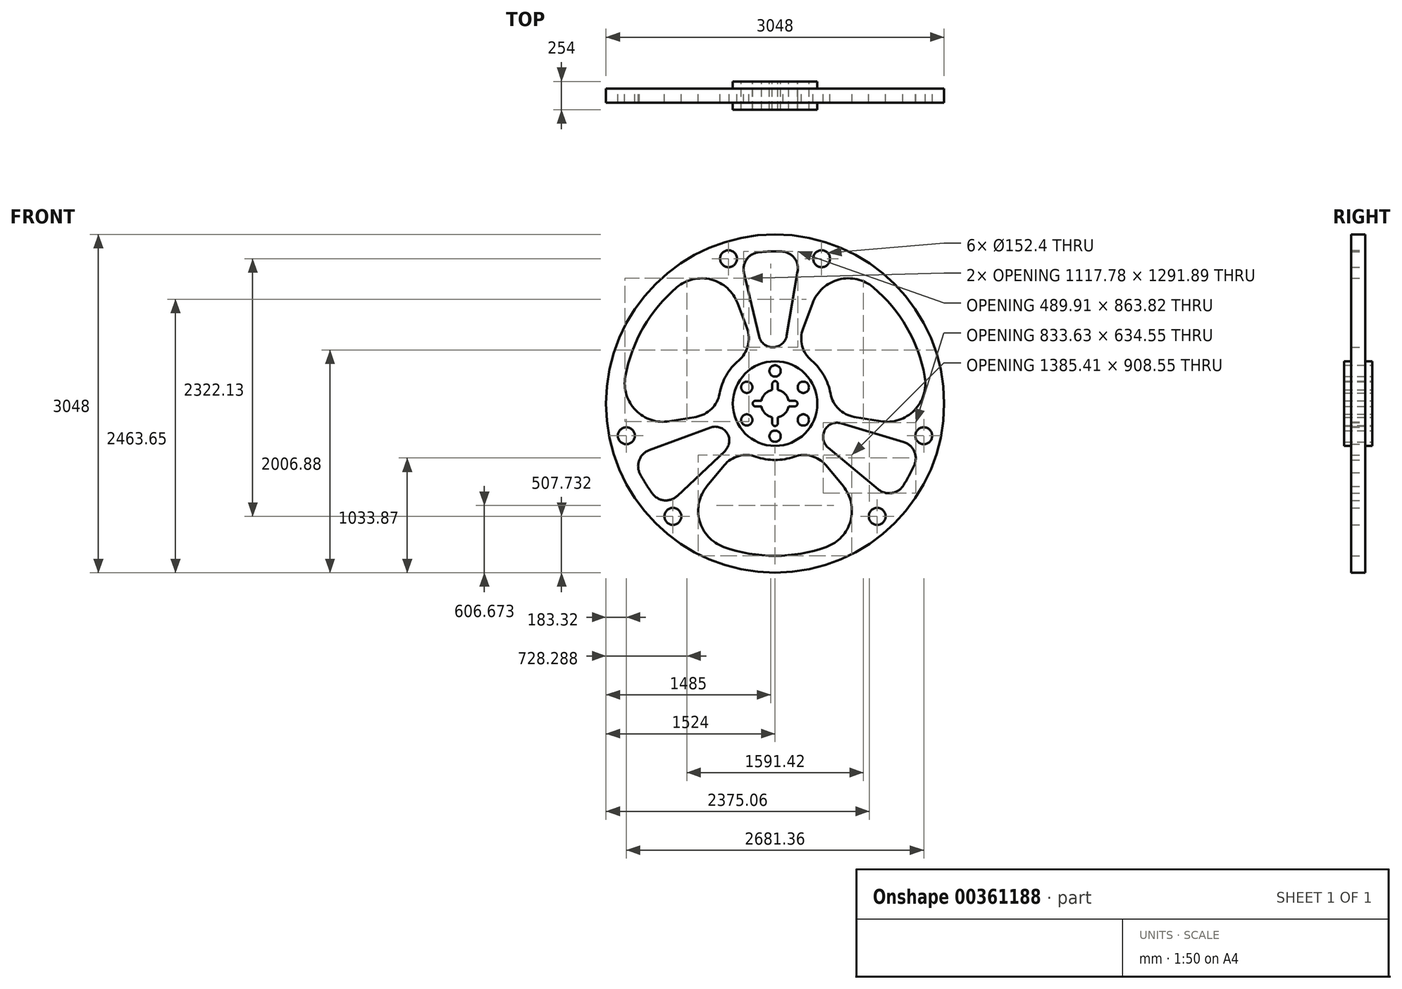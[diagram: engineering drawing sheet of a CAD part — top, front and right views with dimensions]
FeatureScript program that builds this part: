
annotation { "Feature Type Name" : "Feature", "Feature Type Description" : "" }
export const myFeature = defineFeature(function(context is Context, id is Id, definition is map)
    precondition{}
    {
        {
            var Q0;
            Q0=qCreatedBy(makeId("Front.planeOp"),FACE);
            var sketch = newSketch(context, id + "F0", { "sketchPlane" : qUnion([Q0])});
            skCircle(sketch, "E0", {"center": v(0, 0) * mm, "radius": 1524 * mm});
            skLineSegment(sketch, "E1", {"start": v(-143.94, 605.3) * mm, "end": v(-279.86, 1176.82) * mm});
            skLineSegment(sketch, "E2", {"start": v(104.8, 613.28) * mm, "end": v(203.6, 1191.45) * mm});
            skArc(sketch, "E3", {"start": v(-148.04, 1363.59) * mm, "mid": v(-256.1, 1299.96) * mm, "end": v(-279.86, 1176.82) * mm});
            skArc(sketch, "E4.trimOffspring", {"start": v(203.6, 1191.45) * mm, "mid": v(176.34, 1308.8) * mm, "end": v(72.38, 1369.69) * mm});
            skArc(sketch, "E5.trimOffspring", {"start": v(72.38, 1369.69) * mm, "mid": v(-37.95, 1371.07) * mm, "end": v(-148.04, 1363.59) * mm});
            skArc(sketch, "E6", {"start": v(-143.94, 605.3) * mm, "mid": v(-16.31, 507.74) * mm, "end": v(104.8, 613.28) * mm});
            skArc(sketch, "E7", {"start": v(-328.23, 387.72) * mm, "mid": v(-439.94, 254) * mm, "end": v(-499.9, 90.4) * mm});
            skArc(sketch, "E8", {"start": v(-25.4, 123.15) * mm, "mid": v(-88.91, 88.91) * mm, "end": v(-123.15, 25.4) * mm});
            skCircle(sketch, "E9", {"center": v(-419.55, 1305.86) * mm, "radius": 76.2 * mm});
            skCircle(sketch, "E10", {"center": v(419.55, 1305.86) * mm, "radius": 76.2 * mm});
            skCircle(sketch, "E11.1.0", {"center": v(-1340.68, -289.6) * mm, "radius": 76.2 * mm});
            skCircle(sketch, "E11.1.1", {"center": v(-921.13, -1016.27) * mm, "radius": 76.2 * mm});
            skLineSegment(sketch, "E11.1.2", {"start": v(-452.23, -427.3) * mm, "end": v(-879.23, -830.77) * mm});
            skLineSegment(sketch, "E11.1.3", {"start": v(-583.52, -215.88) * mm, "end": v(-1133.62, -419.4) * mm});
            skArc(sketch, "E11.1.4", {"start": v(-1133.62, -419.4) * mm, "mid": v(-1221.62, -501.69) * mm, "end": v(-1222.38, -622.16) * mm});
            skArc(sketch, "E11.1.5", {"start": v(-1222.38, -622.16) * mm, "mid": v(-1168.4, -718.4) * mm, "end": v(-1106.88, -810) * mm});
            skArc(sketch, "E11.1.6", {"start": v(-1106.88, -810) * mm, "mid": v(-997.74, -871.77) * mm, "end": v(-879.23, -830.77) * mm});
            skArc(sketch, "E11.1.7", {"start": v(-452.23, -427.3) * mm, "mid": v(-431.56, -268) * mm, "end": v(-583.52, -215.88) * mm});
            skCircle(sketch, "E11.2.0", {"center": v(921.13, -1016.27) * mm, "radius": 76.2 * mm});
            skCircle(sketch, "E11.2.1", {"center": v(1340.68, -289.6) * mm, "radius": 76.2 * mm});
            skLineSegment(sketch, "E11.2.2", {"start": v(596.17, -177.99) * mm, "end": v(1159.08, -346.05) * mm});
            skLineSegment(sketch, "E11.2.3", {"start": v(478.72, -397.4) * mm, "end": v(930.03, -772.04) * mm});
            skArc(sketch, "E11.2.4", {"start": v(930.03, -772.04) * mm, "mid": v(1045.29, -807.11) * mm, "end": v(1150, -747.53) * mm});
            skArc(sketch, "E11.2.5", {"start": v(1150, -747.53) * mm, "mid": v(1206.36, -652.67) * mm, "end": v(1254.92, -553.59) * mm});
            skArc(sketch, "E11.2.6", {"start": v(1254.92, -553.59) * mm, "mid": v(1253.85, -428.19) * mm, "end": v(1159.08, -346.05) * mm});
            skArc(sketch, "E11.2.7", {"start": v(596.17, -177.99) * mm, "mid": v(447.87, -239.74) * mm, "end": v(478.72, -397.4) * mm});
            skArc(sketch, "E12", {"start": v(459.34, -557.22) * mm, "mid": v(328.02, -472.14) * mm, "end": v(171.66, -478.12) * mm});
            skPoint(sketch, "E13.centerSnap0", {"position": v(0, -964.87) * mm});
            skArc(sketch, "E14", {"start": v(-613.73, -744.52) * mm, "mid": v(-680.45, -1056.72) * mm, "end": v(-463.49, -1290.92) * mm});
            skArc(sketch, "E15.trimOffspring", {"start": v(463.49, -1290.92) * mm, "mid": v(680.45, -1056.72) * mm, "end": v(613.73, -744.52) * mm});
            skArc(sketch, "E16.trimOffspring", {"start": v(-171.66, -478.12) * mm, "mid": v(-328.02, -472.14) * mm, "end": v(-459.34, -557.22) * mm});
            skArc(sketch, "E17.trimOffspring", {"start": v(-463.49, -1290.92) * mm, "mid": v(0, -1371.6) * mm, "end": v(463.49, -1290.92) * mm});
            skLineSegment(sketch, "E18.trimOffspring", {"start": v(-459.34, -557.22) * mm, "end": v(-613.73, -744.52) * mm});
            skLineSegment(sketch, "E19.trimOffspring", {"start": v(459.34, -557.22) * mm, "end": v(613.73, -744.52) * mm});
            skArc(sketch, "E20.1.0", {"start": v(951.64, -159.25) * mm, "mid": v(1255.37, -60.93) * mm, "end": v(1349.71, 244.07) * mm});
            skLineSegment(sketch, "E20.1.1", {"start": v(712.24, -119.19) * mm, "end": v(951.64, -159.25) * mm});
            skArc(sketch, "E20.1.2", {"start": v(499.9, 90.4) * mm, "mid": v(572.9, -48) * mm, "end": v(712.24, -119.19) * mm});
            skArc(sketch, "E20.1.3", {"start": v(252.9, 676.4) * mm, "mid": v(244.88, 520.14) * mm, "end": v(328.23, 387.72) * mm});
            skLineSegment(sketch, "E20.1.4", {"start": v(252.9, 676.4) * mm, "end": v(337.9, 903.77) * mm});
            skArc(sketch, "E20.1.5", {"start": v(1349.71, 244.07) * mm, "mid": v(1187.84, 685.8) * mm, "end": v(886.22, 1046.85) * mm});
            skArc(sketch, "E20.1.6", {"start": v(886.22, 1046.85) * mm, "mid": v(574.92, 1117.65) * mm, "end": v(337.9, 903.77) * mm});
            skArc(sketch, "E20.2.0", {"start": v(-337.9, 903.77) * mm, "mid": v(-574.92, 1117.65) * mm, "end": v(-886.22, 1046.85) * mm});
            skLineSegment(sketch, "E20.2.1", {"start": v(-252.9, 676.4) * mm, "end": v(-337.9, 903.77) * mm});
            skArc(sketch, "E20.2.2", {"start": v(-328.23, 387.72) * mm, "mid": v(-244.88, 520.14) * mm, "end": v(-252.9, 676.4) * mm});
            skArc(sketch, "E20.2.3", {"start": v(-712.24, -119.19) * mm, "mid": v(-572.9, -48) * mm, "end": v(-499.9, 90.4) * mm});
            skLineSegment(sketch, "E20.2.4", {"start": v(-712.24, -119.19) * mm, "end": v(-951.64, -159.25) * mm});
            skArc(sketch, "E20.2.5", {"start": v(-886.22, 1046.85) * mm, "mid": v(-1187.84, 685.8) * mm, "end": v(-1349.71, 244.07) * mm});
            skArc(sketch, "E20.2.6", {"start": v(-1349.71, 244.07) * mm, "mid": v(-1255.37, -60.93) * mm, "end": v(-951.64, -159.25) * mm});
            skArc(sketch, "E21.trimOffspring", {"start": v(499.9, 90.4) * mm, "mid": v(439.94, 254) * mm, "end": v(328.23, 387.72) * mm});
            skArc(sketch, "E22.trimOffspring", {"start": v(-171.66, -478.12) * mm, "mid": v(0, -508) * mm, "end": v(171.66, -478.12) * mm});
            skCircle(sketch, "E23", {"center": v(0, 0) * mm, "radius": 381 * mm});
            skCircle(sketch, "E24", {"center": v(0, 294.12) * mm, "radius": 50.8 * mm});
            skCircle(sketch, "E25.1.0", {"center": v(-254.72, 147.06) * mm, "radius": 50.8 * mm});
            skCircle(sketch, "E25.2.0", {"center": v(-254.72, -147.06) * mm, "radius": 50.8 * mm});
            skCircle(sketch, "E25.3.0", {"center": v(0, -294.12) * mm, "radius": 50.8 * mm});
            skCircle(sketch, "E25.4.0", {"center": v(254.72, -147.06) * mm, "radius": 50.8 * mm});
            skCircle(sketch, "E25.5.0", {"center": v(254.72, 147.06) * mm, "radius": 50.8 * mm});
            skArc(sketch, "E26", {"start": v(25.4, 176.54) * mm, "mid": v(0, 201.94) * mm, "end": v(-25.4, 176.54) * mm});
            skLineSegment(sketch, "E27", {"start": v(-25.4, 176.54) * mm, "end": v(-25.4, 123.15) * mm});
            skLineSegment(sketch, "E28", {"start": v(25.4, 176.54) * mm, "end": v(25.4, 123.15) * mm});
            skArc(sketch, "E29.1.0", {"start": v(-176.54, 25.4) * mm, "mid": v(-201.94, 0) * mm, "end": v(-176.54, -25.4) * mm});
            skLineSegment(sketch, "E29.1.1", {"start": v(-176.54, -25.4) * mm, "end": v(-123.15, -25.4) * mm});
            skLineSegment(sketch, "E29.1.2", {"start": v(-176.54, 25.4) * mm, "end": v(-123.15, 25.4) * mm});
            skArc(sketch, "E29.2.0", {"start": v(-25.4, -176.54) * mm, "mid": v(0, -201.94) * mm, "end": v(25.4, -176.54) * mm});
            skLineSegment(sketch, "E29.2.1", {"start": v(25.4, -176.54) * mm, "end": v(25.4, -123.15) * mm});
            skLineSegment(sketch, "E29.2.2", {"start": v(-25.4, -176.54) * mm, "end": v(-25.4, -123.15) * mm});
            skArc(sketch, "E29.3.0", {"start": v(176.54, -25.4) * mm, "mid": v(201.94, 0) * mm, "end": v(176.54, 25.4) * mm});
            skLineSegment(sketch, "E29.3.1", {"start": v(176.54, 25.4) * mm, "end": v(123.15, 25.4) * mm});
            skLineSegment(sketch, "E29.3.2", {"start": v(176.54, -25.4) * mm, "end": v(123.15, -25.4) * mm});
            skArc(sketch, "E30.trimOffspring", {"start": v(123.15, 25.4) * mm, "mid": v(88.91, 88.91) * mm, "end": v(25.4, 123.15) * mm});
            skArc(sketch, "E31.trimOffspring", {"start": v(-123.15, -25.4) * mm, "mid": v(-88.91, -88.91) * mm, "end": v(-25.4, -123.15) * mm});
            skArc(sketch, "E32.trimOffspring", {"start": v(25.4, -123.15) * mm, "mid": v(88.91, -88.91) * mm, "end": v(123.15, -25.4) * mm});
            skPoint(sketch, "E33.orphan", {"position": v(0, -1929.74) * mm});
            skPoint(sketch, "E34.end.orphan", {"position": v(220.18, 1283.58) * mm});
            skPoint(sketch, "E35.trimOffspring.end.orphan", {"position": v(-364.02, 1530.73) * mm});
            skSolve(sketch);
        }
        {
            var Q0;
            Q0=makeQuery(id+"F0.imprint","IMPRINT",FACE,{"disambiguationData":[TD([[makeQuery(id+"F0.imprint","IMPRINT",EDGE,{"derivedFrom":sQuery(id+"F0.wireOp",EDGE,"E0")}),1.0]])]});
            extrude(context, id + "F1", {"entities" : qUnion([Q0]), "depth" : 127 * mm, "symmetric" : true});
        }
        {
            var Q0;
            Q0=makeQuery(id+"F0.imprint","IMPRINT",FACE,{"disambiguationData":[TD([[makeQuery(id+"F0.imprint","IMPRINT",EDGE,{"derivedFrom":sQuery(id+"F0.wireOp",EDGE,"E8")}),-1.0]])]});
            extrude(context, id + "F2", {"entities" : qUnion([Q0]), "operationType" : NewBodyOperationType.ADD, "depth" : 254 * mm, "symmetric" : true});
        }
    });
